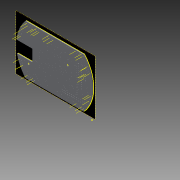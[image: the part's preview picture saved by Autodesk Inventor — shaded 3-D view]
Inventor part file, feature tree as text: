
AUTODESK INVENTOR PART (.ipt)
format: ipt  version: 2014 (Build 180170000, 170)  size: 948,224 bytes
history: native  units: mm
features: other x34, sketch x2, extrude x1
ambient origin geometry x8: Origin, YZ Plane, XZ Plane, XY Plane, X Axis, Y Axis, Z Axis, Center Point
bodies: Volumenkörper1 (feature_tree)
feature tree (37):
  extrude  "Extrusion1"  [1 undecoded]
  other  "Arbeitsachse1"
  other  "Arbeitsachse2"
  other  "Arbeitsachse3"
  other  "Arbeitsachse4"
  other  "Arbeitsachse5"
  other  "Arbeitsachse6"
  other  "Arbeitsachse7"
  other  "Arbeitsachse8"
  other  "Arbeitsachse9"
  other  "Arbeitsachse10"
  other  "Arbeitsachse11"
  other  "Arbeitsachse12"
  other  "Arbeitsachse13"
  other  "Arbeitsachse14"
  other  "Arbeitsachse15"
  other  "Arbeitsachse16"
  other  "Arbeitsachse17"
  other  "Arbeitsachse18"
  other  "Arbeitsachse19"
  other  "Arbeitsachse20"
  other  "Arbeitsachse21"
  other  "Arbeitsachse22"
  other  "Arbeitsachse23"
  other  "Arbeitsachse24"
  other  "Arbeitsachse25"
  other  "Arbeitsachse26"
  other  "Arbeitsachse27"
  other  "Arbeitsachse28"
  other  "Arbeitsachse29"
  other  "Arbeitsachse30"
  other  "Arbeitsachse33"
  other  "Arbeitsachse34"
  other  "Arbeitsachse35"
  sketch  "Skizze3"
  sketch  "Skizze2"  dims[d0=1.5mm d1=0.0mm]
  other  "Bild1"
note: 1 required parameter value undecoded (feature->parameter linkage not recoverable at this tier; creation-order binding heuristic only, values carry confidence <= 0.55)
